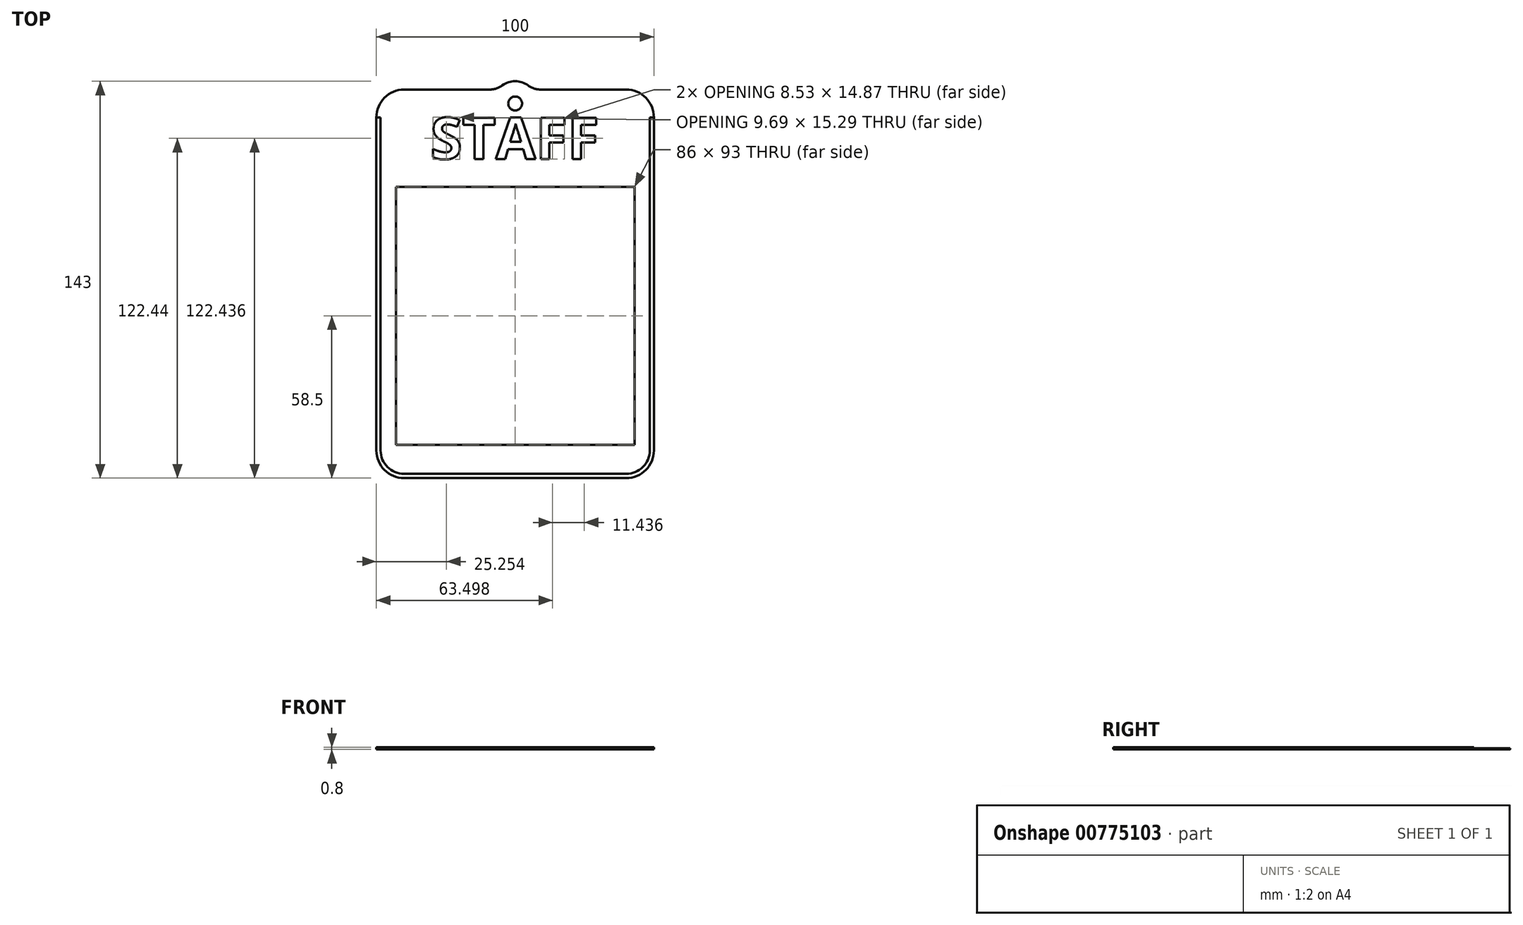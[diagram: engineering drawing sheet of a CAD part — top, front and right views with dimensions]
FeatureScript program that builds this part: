
annotation { "Feature Type Name" : "Feature", "Feature Type Description" : "" }
export const myFeature = defineFeature(function(context is Context, id is Id, definition is map)
    precondition{}
    {
        {
            var Q0;
            Q0=qCreatedBy(makeId("Top.planeOp"),FACE);
            var sketch = newSketch(context, id + "F0", { "sketchPlane" : qUnion([Q0])});
            skLineSegment(sketch, "E0.bottom", {"start": v(-40, 70) * mm, "end": v(-9.33, 70) * mm});
            skLineSegment(sketch, "E0.top", {"start": v(-40, -70) * mm, "end": v(40, -70) * mm});
            skLineSegment(sketch, "E0.left", {"start": v(-50, 60) * mm, "end": v(-50, -60) * mm});
            skLineSegment(sketch, "E0.right", {"start": v(50, 60) * mm, "end": v(50, -60) * mm});
            skPoint(sketch, "E0.middle", {"position": v(0, 0) * mm});
            skCircle(sketch, "E1", {"center": v(0, 65) * mm, "radius": 2.5 * mm});
            skPoint(sketch, "E2.visualSharp", {"position": v(-50, 70) * mm});
            skArc(sketch, "E2.filletArc", {"start": v(-40, 70) * mm, "mid": v(-47.07, 67.07) * mm, "end": v(-50, 60) * mm});
            skPoint(sketch, "E3.visualSharp", {"position": v(50, 70) * mm});
            skArc(sketch, "E3.filletArc", {"start": v(50, 60) * mm, "mid": v(47.07, 67.07) * mm, "end": v(40, 70) * mm});
            skPoint(sketch, "E4.visualSharp", {"position": v(50, -70) * mm});
            skArc(sketch, "E4.filletArc", {"start": v(40, -70) * mm, "mid": v(47.07, -67.07) * mm, "end": v(50, -60) * mm});
            skPoint(sketch, "E5.visualSharp", {"position": v(-50, -70) * mm});
            skArc(sketch, "E5.filletArc", {"start": v(-50, -60) * mm, "mid": v(-47.07, -67.07) * mm, "end": v(-40, -70) * mm});
            skArc(sketch, "E6", {"start": v(-4.66, 71.5) * mm, "mid": v(0, 73) * mm, "end": v(4.66, 71.5) * mm});
            skArc(sketch, "E7.filletArc", {"start": v(-9.33, 70) * mm, "mid": v(-6.88, 70.38) * mm, "end": v(-4.66, 71.5) * mm});
            skLineSegment(sketch, "E8", {"start": v(40, 70) * mm, "end": v(9.33, 70) * mm});
            skArc(sketch, "E9.filletArc", {"start": v(4.66, 71.5) * mm, "mid": v(6.88, 70.38) * mm, "end": v(9.33, 70) * mm});
            skLineSegment(sketch, "E10.bottom", {"start": v(-43, 35) * mm, "end": v(43, 35) * mm});
            skLineSegment(sketch, "E10.top", {"start": v(-43, -58) * mm, "end": v(43, -58) * mm});
            skLineSegment(sketch, "E10.left", {"start": v(-43, 35) * mm, "end": v(-43, -58) * mm});
            skLineSegment(sketch, "E10.right", {"start": v(43, 35) * mm, "end": v(43, -58) * mm});
            skText(sketch, "E11", { "text": "STAFF", "fontName": "OpenSans-Bold.ttf"});
            skLineSegment(sketch, "E12", {"start": v(-40, 70) * mm, "end": v(-40, 35) * mm, "construction": true});
            skPoint(sketch, "E13", {"position": v(-40, 52.5) * mm});
            skPoint(sketch, "E14", {"position": v(-30.55, 52.5) * mm});
            const initialGuessF0  = {"E11": [-0.03055, 0.045, 1, 0, 0.015]};
            skSetInitialGuess(sketch, initialGuessF0);
            skSolve(sketch);
        }
        {
            var Q0;
            Q0=makeQuery(id+"F0.imprint","IMPRINT",FACE,{"disambiguationData":[TD([[makeQuery(id+"F0.imprint","IMPRINT",EDGE,{"derivedFrom":sQuery(id+"F0.wireOp",EDGE,"E0.bottom")}),-1.0]])]});
            var Q1;
            Q1=makeQuery(id+"F0.imprint","IMPRINT",FACE,{"disambiguationData":[TD([[makeQuery(id+"F0.imprint","IMPRINT",EDGE,{"derivedFrom":sQuery(id+"F0.wireOp",EDGE,"E11.sketch_text.stroke-44")}),1.0]])]});
            extrude(context, id + "F1", {"entities" : qUnion([Q0, Q1]), "depth" : 0.4 * mm, "offsetDistance" : 25 * mm, "symmetric" : true});
        }
        {
            var Q0;
            Q0=makeQuery(id+"F0.imprint","IMPRINT",FACE,{"disambiguationData":[TD([[makeQuery(id+"F0.imprint","IMPRINT",EDGE,{"derivedFrom":sQuery(id+"F0.wireOp",EDGE,"E11.sketch_text.stroke-0")}),-1.0]])]});
            var Q1;
            Q1=makeQuery(id+"F0.imprint","IMPRINT",FACE,{"disambiguationData":[TD([[makeQuery(id+"F0.imprint","IMPRINT",EDGE,{"derivedFrom":sQuery(id+"F0.wireOp",EDGE,"E11.sketch_text.stroke-28")}),-1.0]])]});
            var Q2;
            Q2=makeQuery(id+"F0.imprint","IMPRINT",FACE,{"disambiguationData":[TD([[makeQuery(id+"F0.imprint","IMPRINT",EDGE,{"derivedFrom":sQuery(id+"F0.wireOp",EDGE,"E11.sketch_text.stroke-36")}),-1.0]])]});
            var Q3;
            Q3=makeQuery(id+"F0.imprint","IMPRINT",FACE,{"disambiguationData":[TD([[makeQuery(id+"F0.imprint","IMPRINT",EDGE,{"derivedFrom":sQuery(id+"F0.wireOp",EDGE,"E11.sketch_text.stroke-48")}),-1.0]])]});
            var Q4;
            Q4=makeQuery(id+"F0.imprint","IMPRINT",FACE,{"disambiguationData":[TD([[makeQuery(id+"F0.imprint","IMPRINT",EDGE,{"derivedFrom":sQuery(id+"F0.wireOp",EDGE,"E11.sketch_text.stroke-58")}),-1.0]])]});
            var Q5;
            Q5=makeQuery(id+"F1.opExtrude","CAP_FACE",FACE,{"disambiguationData":[OSD([sQuery(id+"F0.wireOp",EDGE,"E0.bottom"),sQuery(id+"F0.wireOp",EDGE,"E0.top"),sQuery(id+"F0.wireOp",EDGE,"E0.left"),sQuery(id+"F0.wireOp",EDGE,"E0.right"),sQuery(id+"F0.wireOp",EDGE,"E1"),sQuery(id+"F0.wireOp",EDGE,"E2.filletArc"),sQuery(id+"F0.wireOp",EDGE,"E3.filletArc"),sQuery(id+"F0.wireOp",EDGE,"E4.filletArc"),sQuery(id+"F0.wireOp",EDGE,"E5.filletArc"),sQuery(id+"F0.wireOp",EDGE,"E6"),sQuery(id+"F0.wireOp",EDGE,"E7.filletArc"),sQuery(id+"F0.wireOp",EDGE,"E8"),sQuery(id+"F0.wireOp",EDGE,"E9.filletArc"),sQuery(id+"F0.wireOp",EDGE,"E10.bottom"),sQuery(id+"F0.wireOp",EDGE,"E10.top"),sQuery(id+"F0.wireOp",EDGE,"E10.left"),sQuery(id+"F0.wireOp",EDGE,"E10.right"),sQuery(id+"F0.wireOp",EDGE,"E11.sketch_text.stroke-0"),sQuery(id+"F0.wireOp",EDGE,"E11.sketch_text.stroke-1"),sQuery(id+"F0.wireOp",EDGE,"E11.sketch_text.stroke-2"),sQuery(id+"F0.wireOp",EDGE,"E11.sketch_text.stroke-3"),sQuery(id+"F0.wireOp",EDGE,"E11.sketch_text.stroke-4"),sQuery(id+"F0.wireOp",EDGE,"E11.sketch_text.stroke-5"),sQuery(id+"F0.wireOp",EDGE,"E11.sketch_text.stroke-6"),sQuery(id+"F0.wireOp",EDGE,"E11.sketch_text.stroke-7"),sQuery(id+"F0.wireOp",EDGE,"E11.sketch_text.stroke-8"),sQuery(id+"F0.wireOp",EDGE,"E11.sketch_text.stroke-9"),sQuery(id+"F0.wireOp",EDGE,"E11.sketch_text.stroke-10"),sQuery(id+"F0.wireOp",EDGE,"E11.sketch_text.stroke-11"),sQuery(id+"F0.wireOp",EDGE,"E11.sketch_text.stroke-12"),sQuery(id+"F0.wireOp",EDGE,"E11.sketch_text.stroke-13"),sQuery(id+"F0.wireOp",EDGE,"E11.sketch_text.stroke-14"),sQuery(id+"F0.wireOp",EDGE,"E11.sketch_text.stroke-15"),sQuery(id+"F0.wireOp",EDGE,"E11.sketch_text.stroke-16"),sQuery(id+"F0.wireOp",EDGE,"E11.sketch_text.stroke-17"),sQuery(id+"F0.wireOp",EDGE,"E11.sketch_text.stroke-18"),sQuery(id+"F0.wireOp",EDGE,"E11.sketch_text.stroke-19"),sQuery(id+"F0.wireOp",EDGE,"E11.sketch_text.stroke-20"),sQuery(id+"F0.wireOp",EDGE,"E11.sketch_text.stroke-21"),sQuery(id+"F0.wireOp",EDGE,"E11.sketch_text.stroke-22"),sQuery(id+"F0.wireOp",EDGE,"E11.sketch_text.stroke-23"),sQuery(id+"F0.wireOp",EDGE,"E11.sketch_text.stroke-24"),sQuery(id+"F0.wireOp",EDGE,"E11.sketch_text.stroke-25"),sQuery(id+"F0.wireOp",EDGE,"E11.sketch_text.stroke-26"),sQuery(id+"F0.wireOp",EDGE,"E11.sketch_text.stroke-27"),sQuery(id+"F0.wireOp",EDGE,"E11.sketch_text.stroke-28"),sQuery(id+"F0.wireOp",EDGE,"E11.sketch_text.stroke-29"),sQuery(id+"F0.wireOp",EDGE,"E11.sketch_text.stroke-30"),sQuery(id+"F0.wireOp",EDGE,"E11.sketch_text.stroke-31"),sQuery(id+"F0.wireOp",EDGE,"E11.sketch_text.stroke-32"),sQuery(id+"F0.wireOp",EDGE,"E11.sketch_text.stroke-33"),sQuery(id+"F0.wireOp",EDGE,"E11.sketch_text.stroke-34"),sQuery(id+"F0.wireOp",EDGE,"E11.sketch_text.stroke-35"),sQuery(id+"F0.wireOp",EDGE,"E11.sketch_text.stroke-36"),sQuery(id+"F0.wireOp",EDGE,"E11.sketch_text.stroke-37"),sQuery(id+"F0.wireOp",EDGE,"E11.sketch_text.stroke-38"),sQuery(id+"F0.wireOp",EDGE,"E11.sketch_text.stroke-39"),sQuery(id+"F0.wireOp",EDGE,"E11.sketch_text.stroke-40"),sQuery(id+"F0.wireOp",EDGE,"E11.sketch_text.stroke-41"),sQuery(id+"F0.wireOp",EDGE,"E11.sketch_text.stroke-42"),sQuery(id+"F0.wireOp",EDGE,"E11.sketch_text.stroke-43"),sQuery(id+"F0.wireOp",EDGE,"E11.sketch_text.stroke-48"),sQuery(id+"F0.wireOp",EDGE,"E11.sketch_text.stroke-49"),sQuery(id+"F0.wireOp",EDGE,"E11.sketch_text.stroke-50"),sQuery(id+"F0.wireOp",EDGE,"E11.sketch_text.stroke-51"),sQuery(id+"F0.wireOp",EDGE,"E11.sketch_text.stroke-52"),sQuery(id+"F0.wireOp",EDGE,"E11.sketch_text.stroke-53"),sQuery(id+"F0.wireOp",EDGE,"E11.sketch_text.stroke-54"),sQuery(id+"F0.wireOp",EDGE,"E11.sketch_text.stroke-55"),sQuery(id+"F0.wireOp",EDGE,"E11.sketch_text.stroke-56"),sQuery(id+"F0.wireOp",EDGE,"E11.sketch_text.stroke-57"),sQuery(id+"F0.wireOp",EDGE,"E11.sketch_text.stroke-58"),sQuery(id+"F0.wireOp",EDGE,"E11.sketch_text.stroke-59"),sQuery(id+"F0.wireOp",EDGE,"E11.sketch_text.stroke-60"),sQuery(id+"F0.wireOp",EDGE,"E11.sketch_text.stroke-61"),sQuery(id+"F0.wireOp",EDGE,"E11.sketch_text.stroke-62"),sQuery(id+"F0.wireOp",EDGE,"E11.sketch_text.stroke-63"),sQuery(id+"F0.wireOp",EDGE,"E11.sketch_text.stroke-64"),sQuery(id+"F0.wireOp",EDGE,"E11.sketch_text.stroke-65"),sQuery(id+"F0.wireOp",EDGE,"E11.sketch_text.stroke-66"),sQuery(id+"F0.wireOp",EDGE,"E11.sketch_text.stroke-67")])],"isStart":false});
            extrude(context, id + "F2", {"entities" : qUnion([Q0, Q1, Q2, Q3, Q4]), "endBound" : BoundingType.UP_TO_SURFACE, "depth" : 25 * mm, "endBoundEntityFace" : qUnion([Q5]), "offsetDistance" : 25 * mm});
        }
        {
            var Q0;
            Q0=makeQuery(id+"F1.opExtrude","CAP_FACE",FACE,{"disambiguationData":[OSD([sQuery(id+"F0.wireOp",EDGE,"E0.bottom"),sQuery(id+"F0.wireOp",EDGE,"E0.top"),sQuery(id+"F0.wireOp",EDGE,"E0.left"),sQuery(id+"F0.wireOp",EDGE,"E0.right"),sQuery(id+"F0.wireOp",EDGE,"E1"),sQuery(id+"F0.wireOp",EDGE,"E2.filletArc"),sQuery(id+"F0.wireOp",EDGE,"E3.filletArc"),sQuery(id+"F0.wireOp",EDGE,"E4.filletArc"),sQuery(id+"F0.wireOp",EDGE,"E5.filletArc"),sQuery(id+"F0.wireOp",EDGE,"E6"),sQuery(id+"F0.wireOp",EDGE,"E7.filletArc"),sQuery(id+"F0.wireOp",EDGE,"E8"),sQuery(id+"F0.wireOp",EDGE,"E9.filletArc"),sQuery(id+"F0.wireOp",EDGE,"E10.bottom"),sQuery(id+"F0.wireOp",EDGE,"E10.top"),sQuery(id+"F0.wireOp",EDGE,"E10.left"),sQuery(id+"F0.wireOp",EDGE,"E10.right")])],"isStart":false});
            var sketch = newSketch(context, id + "F3", { "sketchPlane" : qUnion([Q0])});
            skLineSegment(sketch, "E15.0", {"start": v(-48.5, 60) * mm, "end": v(-48.5, -60) * mm});
            skLineSegment(sketch, "E15.1", {"start": v(48.5, 60) * mm, "end": v(48.5, -60) * mm});
            skArc(sketch, "E15.2", {"start": v(40, -68.5) * mm, "mid": v(46.01, -66.01) * mm, "end": v(48.5, -60) * mm});
            skLineSegment(sketch, "E15.3", {"start": v(-40, -68.5) * mm, "end": v(40, -68.5) * mm});
            skArc(sketch, "E15.4", {"start": v(-48.5, -60) * mm, "mid": v(-46.01, -66.01) * mm, "end": v(-40, -68.5) * mm});
            skLineSegment(sketch, "E16", {"start": v(-48.5, 60) * mm, "end": v(-50, 60) * mm});
            skLineSegment(sketch, "E17", {"start": v(48.5, 60) * mm, "end": v(50, 60) * mm});
            skSolve(sketch);
        }
        {
            var Q0;
            Q0=makeQuery(id+"F3.imprint","IMPRINT",FACE,{"disambiguationData":[TD([[makeQuery(id+"F3.imprint","IMPRINT",EDGE,{"derivedFrom":sQuery(id+"F3.wireOp",EDGE,"E15.0")}),-1.0]])]});
            extrude(context, id + "F4", {"entities" : qUnion([Q0]), "operationType" : NewBodyOperationType.ADD, "depth" : .4 * mm, "offsetDistance" : 25 * mm});
        }
    });
